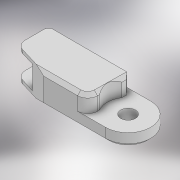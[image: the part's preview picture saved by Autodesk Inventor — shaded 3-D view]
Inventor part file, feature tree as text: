
AUTODESK INVENTOR PART (.ipt)
format: ipt  version: 2022 (Build 260153000, 153)  size: 222,208 bytes
history: native  units: mm
features: sketch x7, extrude x7, projected_geometry x5, chamfer x3, fillet x2
ambient origin geometry x8: Origin, YZ Plane, XZ Plane, XY Plane, X Axis, Y Axis, Z Axis, Center Point
bodies: Solid1 (feature_tree)
feature tree (24):
  sketch  "Sketch2"  dims[d0=4.4mm d1=13.5mm]
  extrude  "Extrusion1"  Depth=13.5mm
  extrude  "Extrusion2"  Depth=8.85mm TaperAngle=0.0deg
  extrude  "Extrusion3"  Depth=1.0mm
  extrude  "Extrusion4"  Depth=8.85mm TaperAngle=0.0deg
  extrude  "Extrusion5"  Depth=8.0mm TaperAngle=0.0deg
  extrude  "Extrusion6"  Depth=8.0mm TaperAngle=0.0deg
  extrude  "Extrusion7"  Depth=1.0mm TaperAngle=0.0deg
  sketch  "Sketch8"  dims[d17=10.25mm d18=0.0mm d19=10.25mm d20=0.0mm d21=3.0mm d22=2.0mm d23=2.0mm d24=45.0deg d25=2.0mm d26=2.0mm d27=45.0deg d28=3.0mm d29=1.0mm d30=2.0mm d31=45.0deg]
  fillet  "Fillet1"  Radius=3.0mm
  chamfer  "Chamfer1"  Distance=2.0mm Angle=45.0deg
  chamfer  "Chamfer2"  Distance=2.0mm Angle=45.0deg
  fillet  "Fillet2"  Radius=3.0mm
  chamfer  "Chamfer3"  Distance=1.0mm Angle=45.0deg
  sketch  "Sketch3"  dims[d2=3.85mm d3=0.0mm d4=8.85mm d5=0.0mm]
  projected_geometry  "Projected Loop1"
  sketch  "Sketch4"  dims[d6=0.5mm d7=1.0mm]
  projected_geometry  "Projected Loop2"
  sketch  "Sketch5"  dims[d8=12.5mm d9=8.85mm d10=0.0mm]
  projected_geometry  "Projected Loop3"
  sketch  "Sketch6"  dims[d11=1.0mm d12=8.0mm d13=0.0mm]
  sketch  "Sketch7"  dims[d14=5.1mm d15=8.0mm d16=0.0mm]
  projected_geometry  "Projected Loop5"
  projected_geometry  "Projected Loop6"
